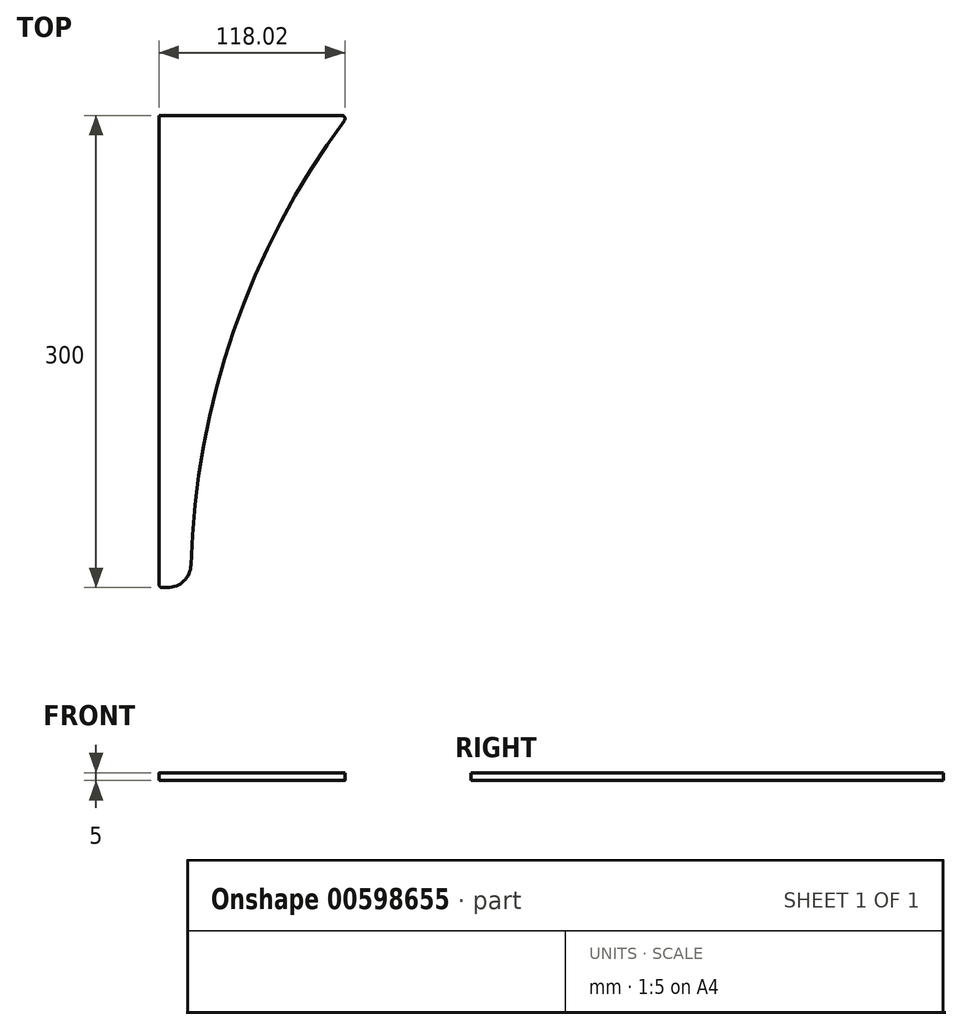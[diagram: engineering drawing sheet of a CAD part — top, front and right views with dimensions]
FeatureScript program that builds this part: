
annotation { "Feature Type Name" : "Feature", "Feature Type Description" : "" }
export const myFeature = defineFeature(function(context is Context, id is Id, definition is map)
    precondition{}
    {
        {
            var Q0;
            Q0=qCreatedBy(makeId("Top.planeOp"),FACE);
            var sketch = newSketch(context, id + "F0", { "sketchPlane" : qUnion([Q0])});
            skLineSegment(sketch, "E0", {"start": v(250, 300) * mm, "end": v(370, 300) * mm});
            skLineSegment(sketch, "E1", {"start": v(0, 0) * mm, "end": v(0, 300) * mm, "construction": true});
            skLineSegment(sketch, "E2", {"start": v(250, 0) * mm, "end": v(270, 0) * mm});
            skArc(sketch, "E3", {"start": v(370, 300) * mm, "mid": v(295.66, 158.11) * mm, "end": v(270, 0) * mm});
            skLineSegment(sketch, "E4", {"start": v(250, 300) * mm, "end": v(250, 0) * mm});
            skPoint(sketch, "E5.orphan", {"position": v(375, 280) * mm});
            skPoint(sketch, "E6.end.orphan", {"position": v(375, 320) * mm});
            skLineSegment(sketch, "E7", {"start": v(375, 320) * mm, "end": v(375, 280) * mm, "construction": true});
            skCircle(sketch, "E8", {"center": v(294.63, 255.37) * mm, "radius": 19.63 * mm});
            skSolve(sketch);
        }
        {
            var Q0;
            Q0=makeQuery(id+"F0.imprint","IMPRINT",FACE,{"disambiguationData":[TD([[makeQuery(id+"F0.imprint","IMPRINT",EDGE,{"derivedFrom":sQuery(id+"F0.wireOp",EDGE,"E0")}),-1.0]])]});
            var Q1;
            Q1=makeQuery(id+"F0.imprint","IMPRINT",FACE,{"disambiguationData":[TD([[makeQuery(id+"F0.imprint","IMPRINT",EDGE,{"derivedFrom":sQuery(id+"F0.wireOp",EDGE,"E8")}),1.0]])]});
            extrude(context, id + "F1", {"entities" : qUnion([Q0, Q1]), "endBound" : BoundingType.SYMMETRIC, "depth" : 5 * mm, "offsetDistance" : 25 * mm});
        }
        {
            var Q0;
            Q0=makeQuery(id+"F1.opExtrude","SWEPT_EDGE",EDGE,{"disambiguationData":[OSD([sQuery(id+"F0.wireOp",EDGE,"E2"),sQuery(id+"F0.wireOp",EDGE,"E4")])]});
            var Q1;
            Q1=makeQuery(id+"F1.opExtrude","SWEPT_EDGE",EDGE,{"disambiguationData":[OSD([sQuery(id+"F0.wireOp",EDGE,"E0"),sQuery(id+"F0.wireOp",EDGE,"E3")])]});
            fillet(context, id + "F2", {"entities" : qUnion([Q0, Q1]), "radius" : 2 * mm, "tangentPropagation" : true, "allowEdgeOverflow" : false});
        }
        {
            var Q0;
            Q0=makeQuery(id+"F1.opExtrude","SWEPT_EDGE",EDGE,{"disambiguationData":[OSD([sQuery(id+"F0.wireOp",EDGE,"E2"),sQuery(id+"F0.wireOp",EDGE,"E3")])]});
            fillet(context, id + "F3", {"entities" : qUnion([Q0]), "radius" : 15 * mm, "tangentPropagation" : true, "allowEdgeOverflow" : false});
        }
    });
